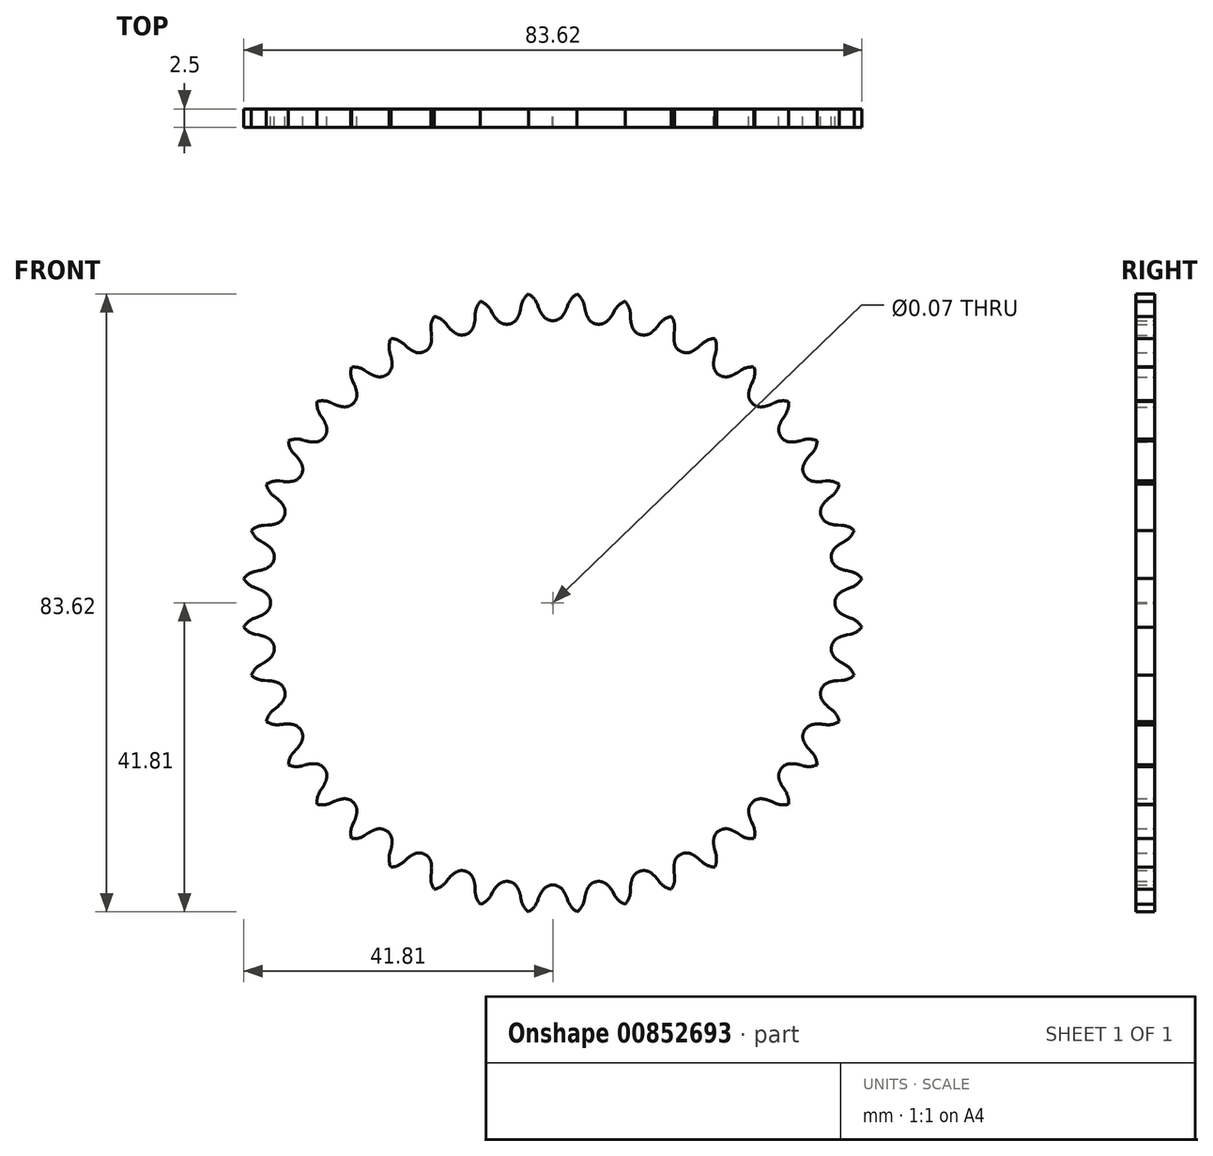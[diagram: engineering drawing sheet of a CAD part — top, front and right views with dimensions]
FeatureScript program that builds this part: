
annotation { "Feature Type Name" : "Feature", "Feature Type Description" : "" }
export const myFeature = defineFeature(function(context is Context, id is Id, definition is map)
    precondition{}
    {
        {
            var Q0;
            Q0=qCreatedBy(makeId("Front.planeOp"),FACE);
            var sketch = newSketch(context, id + "F0", { "sketchPlane" : qUnion([Q0]), "disableImprinting" : false});
            skCircle(sketch, "E0", {"center": v(0, 0) * mm, "radius": 0.04 * mm});
            skCircle(sketch, "E1", {"center": v(0, 0) * mm, "radius": 39.83 * mm, "construction": true});
            skLineSegment(sketch, "E2", {"start": v(0, 0) * mm, "end": v(0, 79.66) * mm, "construction": true});
            skLineSegment(sketch, "E3", {"start": v(-1.28, 39.83) * mm, "end": v(0, 39.83) * mm, "construction": true});
            skArc(sketch, "E4", {"start": v(-1.33, 38.84) * mm, "mid": v(-0.75, 38.35) * mm, "end": v(0, 38.17) * mm});
            skLineSegment(sketch, "E5.0", {"start": v(2.12, 0) * mm, "end": v(2.12, 79.66) * mm, "construction": true});
            skLineSegment(sketch, "E6.0", {"start": v(-1.75, 41.4) * mm, "end": v(1.4, 41.4) * mm, "construction": true});
            skLineSegment(sketch, "E7", {"start": v(2.57, 41.73) * mm, "end": v(-1.33, 38.84) * mm, "construction": true});
            skPoint(sketch, "E8", {"position": v(2.12, 41.4) * mm});
            skLineSegment(sketch, "E9", {"start": v(-1.92, 39.94) * mm, "end": v(2.12, 41.4) * mm, "construction": true});
            skArc(sketch, "E10", {"start": v(-1.92, 39.94) * mm, "mid": v(-1.67, 39.37) * mm, "end": v(-1.33, 38.84) * mm});
            skLineSegment(sketch, "E11", {"start": v(-1.92, 39.94) * mm, "end": v(-2.08, 40.38) * mm});
            skLineSegment(sketch, "E12.0", {"start": v(-4.6, 0) * mm, "end": v(-4.6, 79.66) * mm, "construction": true});
            skLineSegment(sketch, "E13.0", {"start": v(-3.1, 39.47) * mm, "end": v(0, 39.47) * mm, "construction": true});
            skArc(sketch, "E14", {"start": v(-4.6, 42.15) * mm, "mid": v(-6.5, 37.57) * mm, "end": v(-1.92, 39.47) * mm, "construction": true});
            skLineSegment(sketch, "E15", {"start": v(0, 0) * mm, "end": v(-0.91, 11.62) * mm, "construction": true});
            skLineSegment(sketch, "E16.trimOffspring", {"start": v(-1.7, 39.3) * mm, "end": v(-2.45, 41.4) * mm});
            skArc(sketch, "E17.trimOffspring", {"start": v(-2.08, 40.38) * mm, "mid": v(-2.56, 41.2) * mm, "end": v(-3.3, 41.8) * mm});
            skArc(sketch, "E18.trimOffspring", {"start": v(-1.94, 39.78) * mm, "mid": v(-1.94, 39.8) * mm, "end": v(-1.95, 39.83) * mm, "construction": true});
            skArc(sketch, "E19.trimOffspring", {"start": v(1.66, 39.8) * mm, "mid": v(-0.17, 41.48) * mm, "end": v(-1.62, 39.47) * mm, "construction": true});
            skArc(sketch, "E20.MirrorCS", {"start": v(1.33, 38.84) * mm, "mid": v(0.75, 38.35) * mm, "end": v(0, 38.17) * mm});
            skArc(sketch, "E21.MirrorCS", {"start": v(1.92, 39.94) * mm, "mid": v(1.67, 39.37) * mm, "end": v(1.33, 38.84) * mm});
            skLineSegment(sketch, "E22.MirrorCS", {"start": v(1.92, 39.94) * mm, "end": v(2.08, 40.38) * mm});
            skArc(sketch, "E23.MirrorCS", {"start": v(2.08, 40.38) * mm, "mid": v(2.56, 41.2) * mm, "end": v(3.3, 41.8) * mm});
            skArc(sketch, "E24.1.0", {"start": v(-8.37, 39.56) * mm, "mid": v(-8.97, 40.3) * mm, "end": v(-9.79, 40.78) * mm});
            skLineSegment(sketch, "E24.1.1", {"start": v(-8.14, 39.14) * mm, "end": v(-8.37, 39.56) * mm});
            skArc(sketch, "E24.1.2", {"start": v(-8.14, 39.14) * mm, "mid": v(-7.8, 38.62) * mm, "end": v(-7.4, 38.16) * mm});
            skArc(sketch, "E24.1.3", {"start": v(-7.4, 38.16) * mm, "mid": v(-6.74, 37.76) * mm, "end": v(-5.97, 37.7) * mm});
            skArc(sketch, "E24.1.4", {"start": v(-4.76, 38.57) * mm, "mid": v(-5.26, 38) * mm, "end": v(-5.97, 37.7) * mm});
            skArc(sketch, "E24.1.5", {"start": v(-4.35, 39.75) * mm, "mid": v(-4.51, 39.14) * mm, "end": v(-4.76, 38.57) * mm});
            skLineSegment(sketch, "E24.1.6", {"start": v(-4.35, 39.75) * mm, "end": v(-4.26, 40.2) * mm});
            skArc(sketch, "E24.1.7", {"start": v(-4.26, 40.2) * mm, "mid": v(-3.92, 41.1) * mm, "end": v(-3.3, 41.8) * mm});
            skArc(sketch, "E24.2.0", {"start": v(-14.46, 37.76) * mm, "mid": v(-15.16, 38.4) * mm, "end": v(-16.05, 38.74) * mm});
            skLineSegment(sketch, "E24.2.1", {"start": v(-14.17, 37.39) * mm, "end": v(-14.46, 37.76) * mm});
            skArc(sketch, "E24.2.2", {"start": v(-14.17, 37.39) * mm, "mid": v(-13.75, 36.93) * mm, "end": v(-13.27, 36.53) * mm});
            skArc(sketch, "E24.2.3", {"start": v(-13.27, 36.53) * mm, "mid": v(-12.56, 36.24) * mm, "end": v(-11.8, 36.3) * mm});
            skArc(sketch, "E24.2.4", {"start": v(-10.73, 37.35) * mm, "mid": v(-11.14, 36.7) * mm, "end": v(-11.8, 36.3) * mm});
            skArc(sketch, "E24.2.5", {"start": v(-10.51, 38.58) * mm, "mid": v(-10.58, 37.96) * mm, "end": v(-10.73, 37.35) * mm});
            skLineSegment(sketch, "E24.2.6", {"start": v(-10.51, 38.58) * mm, "end": v(-10.5, 39.05) * mm});
            skArc(sketch, "E24.2.7", {"start": v(-10.5, 39.05) * mm, "mid": v(-10.3, 39.98) * mm, "end": v(-9.79, 40.78) * mm});
            skArc(sketch, "E24.3.0", {"start": v(-20.19, 35.03) * mm, "mid": v(-20.98, 35.55) * mm, "end": v(-21.91, 35.76) * mm});
            skLineSegment(sketch, "E24.3.1", {"start": v(-19.84, 34.71) * mm, "end": v(-20.19, 35.03) * mm});
            skArc(sketch, "E24.3.2", {"start": v(-19.84, 34.71) * mm, "mid": v(-19.36, 34.32) * mm, "end": v(-18.82, 34) * mm});
            skArc(sketch, "E24.3.3", {"start": v(-18.82, 34) * mm, "mid": v(-18.08, 33.83) * mm, "end": v(-17.33, 34) * mm});
            skArc(sketch, "E24.3.4", {"start": v(-16.45, 35.21) * mm, "mid": v(-16.74, 34.5) * mm, "end": v(-17.33, 34) * mm});
            skArc(sketch, "E24.3.5", {"start": v(-16.42, 36.46) * mm, "mid": v(-16.39, 35.83) * mm, "end": v(-16.45, 35.21) * mm});
            skLineSegment(sketch, "E24.3.6", {"start": v(-16.42, 36.46) * mm, "end": v(-16.48, 36.92) * mm});
            skArc(sketch, "E24.3.7", {"start": v(-16.48, 36.92) * mm, "mid": v(-16.43, 37.87) * mm, "end": v(-16.05, 38.74) * mm});
            skArc(sketch, "E24.4.0", {"start": v(-25.42, 31.45) * mm, "mid": v(-26.29, 31.83) * mm, "end": v(-27.24, 31.89) * mm});
            skLineSegment(sketch, "E24.4.1", {"start": v(-25.03, 31.18) * mm, "end": v(-25.42, 31.45) * mm});
            skArc(sketch, "E24.4.2", {"start": v(-25.03, 31.18) * mm, "mid": v(-24.49, 30.87) * mm, "end": v(-23.91, 30.64) * mm});
            skArc(sketch, "E24.4.3", {"start": v(-23.91, 30.64) * mm, "mid": v(-23.14, 30.58) * mm, "end": v(-22.44, 30.88) * mm});
            skArc(sketch, "E24.4.4", {"start": v(-21.75, 32.2) * mm, "mid": v(-21.94, 31.46) * mm, "end": v(-22.44, 30.88) * mm});
            skArc(sketch, "E24.4.5", {"start": v(-21.92, 33.44) * mm, "mid": v(-21.8, 32.83) * mm, "end": v(-21.75, 32.2) * mm});
            skLineSegment(sketch, "E24.4.6", {"start": v(-21.92, 33.44) * mm, "end": v(-22.05, 33.9) * mm});
            skArc(sketch, "E24.4.7", {"start": v(-22.05, 33.9) * mm, "mid": v(-22.15, 34.84) * mm, "end": v(-21.91, 35.76) * mm});
            skArc(sketch, "E24.5.0", {"start": v(-30.03, 27.08) * mm, "mid": v(-30.94, 27.33) * mm, "end": v(-31.89, 27.24) * mm});
            skLineSegment(sketch, "E24.5.1", {"start": v(-29.6, 26.88) * mm, "end": v(-30.03, 27.08) * mm});
            skArc(sketch, "E24.5.2", {"start": v(-29.6, 26.88) * mm, "mid": v(-29.02, 26.66) * mm, "end": v(-28.4, 26.52) * mm});
            skArc(sketch, "E24.5.3", {"start": v(-28.4, 26.52) * mm, "mid": v(-27.64, 26.59) * mm, "end": v(-27, 27) * mm});
            skArc(sketch, "E24.5.4", {"start": v(-26.52, 28.4) * mm, "mid": v(-26.59, 27.64) * mm, "end": v(-27, 27) * mm});
            skArc(sketch, "E24.5.5", {"start": v(-26.88, 29.6) * mm, "mid": v(-26.66, 29.02) * mm, "end": v(-26.52, 28.4) * mm});
            skLineSegment(sketch, "E24.5.6", {"start": v(-26.88, 29.6) * mm, "end": v(-27.08, 30.03) * mm});
            skArc(sketch, "E24.5.7", {"start": v(-27.08, 30.03) * mm, "mid": v(-27.33, 30.94) * mm, "end": v(-27.24, 31.89) * mm});
            skArc(sketch, "E24.6.0", {"start": v(-33.9, 22.05) * mm, "mid": v(-34.84, 22.15) * mm, "end": v(-35.76, 21.91) * mm});
            skLineSegment(sketch, "E24.6.1", {"start": v(-33.44, 21.92) * mm, "end": v(-33.9, 22.05) * mm});
            skArc(sketch, "E24.6.2", {"start": v(-33.44, 21.92) * mm, "mid": v(-32.83, 21.8) * mm, "end": v(-32.2, 21.75) * mm});
            skArc(sketch, "E24.6.3", {"start": v(-32.2, 21.75) * mm, "mid": v(-31.46, 21.94) * mm, "end": v(-30.88, 22.44) * mm});
            skArc(sketch, "E24.6.4", {"start": v(-30.64, 23.91) * mm, "mid": v(-30.58, 23.14) * mm, "end": v(-30.88, 22.44) * mm});
            skArc(sketch, "E24.6.5", {"start": v(-31.18, 25.03) * mm, "mid": v(-30.87, 24.49) * mm, "end": v(-30.64, 23.91) * mm});
            skLineSegment(sketch, "E24.6.6", {"start": v(-31.18, 25.03) * mm, "end": v(-31.45, 25.42) * mm});
            skArc(sketch, "E24.6.7", {"start": v(-31.45, 25.42) * mm, "mid": v(-31.83, 26.29) * mm, "end": v(-31.89, 27.24) * mm});
            skArc(sketch, "E24.7.0", {"start": v(-36.92, 16.48) * mm, "mid": v(-37.87, 16.43) * mm, "end": v(-38.74, 16.05) * mm});
            skLineSegment(sketch, "E24.7.1", {"start": v(-36.46, 16.42) * mm, "end": v(-36.92, 16.48) * mm});
            skArc(sketch, "E24.7.2", {"start": v(-36.46, 16.42) * mm, "mid": v(-35.83, 16.39) * mm, "end": v(-35.21, 16.45) * mm});
            skArc(sketch, "E24.7.3", {"start": v(-35.21, 16.45) * mm, "mid": v(-34.5, 16.74) * mm, "end": v(-34, 17.33) * mm});
            skArc(sketch, "E24.7.4", {"start": v(-34, 18.82) * mm, "mid": v(-33.83, 18.08) * mm, "end": v(-34, 17.33) * mm});
            skArc(sketch, "E24.7.5", {"start": v(-34.71, 19.84) * mm, "mid": v(-34.32, 19.36) * mm, "end": v(-34, 18.82) * mm});
            skLineSegment(sketch, "E24.7.6", {"start": v(-34.71, 19.84) * mm, "end": v(-35.03, 20.19) * mm});
            skArc(sketch, "E24.7.7", {"start": v(-35.03, 20.19) * mm, "mid": v(-35.55, 20.98) * mm, "end": v(-35.76, 21.91) * mm});
            skArc(sketch, "E24.8.0", {"start": v(-39.05, 10.5) * mm, "mid": v(-39.98, 10.3) * mm, "end": v(-40.78, 9.79) * mm});
            skLineSegment(sketch, "E24.8.1", {"start": v(-38.58, 10.51) * mm, "end": v(-39.05, 10.5) * mm});
            skArc(sketch, "E24.8.2", {"start": v(-38.58, 10.51) * mm, "mid": v(-37.96, 10.58) * mm, "end": v(-37.35, 10.73) * mm});
            skArc(sketch, "E24.8.3", {"start": v(-37.35, 10.73) * mm, "mid": v(-36.7, 11.14) * mm, "end": v(-36.3, 11.8) * mm});
            skArc(sketch, "E24.8.4", {"start": v(-36.53, 13.27) * mm, "mid": v(-36.24, 12.56) * mm, "end": v(-36.3, 11.8) * mm});
            skArc(sketch, "E24.8.5", {"start": v(-37.39, 14.17) * mm, "mid": v(-36.93, 13.75) * mm, "end": v(-36.53, 13.27) * mm});
            skLineSegment(sketch, "E24.8.6", {"start": v(-37.39, 14.17) * mm, "end": v(-37.76, 14.46) * mm});
            skArc(sketch, "E24.8.7", {"start": v(-37.76, 14.46) * mm, "mid": v(-38.4, 15.16) * mm, "end": v(-38.74, 16.05) * mm});
            skArc(sketch, "E24.9.0", {"start": v(-40.2, 4.26) * mm, "mid": v(-41.1, 3.92) * mm, "end": v(-41.8, 3.3) * mm});
            skLineSegment(sketch, "E24.9.1", {"start": v(-39.75, 4.35) * mm, "end": v(-40.2, 4.26) * mm});
            skArc(sketch, "E24.9.2", {"start": v(-39.75, 4.35) * mm, "mid": v(-39.14, 4.51) * mm, "end": v(-38.57, 4.76) * mm});
            skArc(sketch, "E24.9.3", {"start": v(-38.57, 4.76) * mm, "mid": v(-38, 5.26) * mm, "end": v(-37.7, 5.97) * mm});
            skArc(sketch, "E24.9.4", {"start": v(-38.16, 7.4) * mm, "mid": v(-37.76, 6.74) * mm, "end": v(-37.7, 5.97) * mm});
            skArc(sketch, "E24.9.5", {"start": v(-39.14, 8.14) * mm, "mid": v(-38.62, 7.8) * mm, "end": v(-38.16, 7.4) * mm});
            skLineSegment(sketch, "E24.9.6", {"start": v(-39.14, 8.14) * mm, "end": v(-39.56, 8.37) * mm});
            skArc(sketch, "E24.9.7", {"start": v(-39.56, 8.37) * mm, "mid": v(-40.3, 8.97) * mm, "end": v(-40.78, 9.79) * mm});
            skLineSegment(sketch, "E25.4.10.0", {"start": v(-39.94, -1.92) * mm, "end": v(-40.38, -2.08) * mm});
            skArc(sketch, "E25.7.10.0", {"start": v(-39.94, -1.92) * mm, "mid": v(-39.37, -1.67) * mm, "end": v(-38.84, -1.33) * mm});
            skArc(sketch, "E25.11.10.0", {"start": v(-38.84, -1.33) * mm, "mid": v(-38.35, -0.75) * mm, "end": v(-38.17, 0) * mm});
            skArc(sketch, "E25.14.10.0", {"start": v(-40.38, -2.08) * mm, "mid": v(-41.2, -2.56) * mm, "end": v(-41.8, -3.3) * mm});
            skArc(sketch, "E25.15.10.0", {"start": v(-38.84, 1.33) * mm, "mid": v(-38.35, 0.75) * mm, "end": v(-38.17, 0) * mm});
            skArc(sketch, "E25.19.10.0", {"start": v(-39.94, 1.92) * mm, "mid": v(-39.37, 1.67) * mm, "end": v(-38.84, 1.33) * mm});
            skLineSegment(sketch, "E25.23.10.0", {"start": v(-39.94, 1.92) * mm, "end": v(-40.38, 2.08) * mm});
            skArc(sketch, "E25.26.10.0", {"start": v(-40.38, 2.08) * mm, "mid": v(-41.2, 2.56) * mm, "end": v(-41.8, 3.3) * mm});
            skLineSegment(sketch, "E25.4.11.0", {"start": v(-39.14, -8.14) * mm, "end": v(-39.56, -8.37) * mm});
            skArc(sketch, "E25.7.11.0", {"start": v(-39.14, -8.14) * mm, "mid": v(-38.62, -7.8) * mm, "end": v(-38.16, -7.4) * mm});
            skArc(sketch, "E25.11.11.0", {"start": v(-38.16, -7.4) * mm, "mid": v(-37.76, -6.74) * mm, "end": v(-37.7, -5.97) * mm});
            skArc(sketch, "E25.14.11.0", {"start": v(-39.56, -8.37) * mm, "mid": v(-40.3, -8.97) * mm, "end": v(-40.78, -9.79) * mm});
            skArc(sketch, "E25.15.11.0", {"start": v(-38.57, -4.76) * mm, "mid": v(-38, -5.26) * mm, "end": v(-37.7, -5.97) * mm});
            skArc(sketch, "E25.19.11.0", {"start": v(-39.75, -4.35) * mm, "mid": v(-39.14, -4.51) * mm, "end": v(-38.57, -4.76) * mm});
            skLineSegment(sketch, "E25.23.11.0", {"start": v(-39.75, -4.35) * mm, "end": v(-40.2, -4.26) * mm});
            skArc(sketch, "E25.26.11.0", {"start": v(-40.2, -4.26) * mm, "mid": v(-41.1, -3.92) * mm, "end": v(-41.8, -3.3) * mm});
            skLineSegment(sketch, "E25.4.12.0", {"start": v(-37.39, -14.17) * mm, "end": v(-37.76, -14.46) * mm});
            skArc(sketch, "E25.7.12.0", {"start": v(-37.39, -14.17) * mm, "mid": v(-36.93, -13.75) * mm, "end": v(-36.53, -13.27) * mm});
            skArc(sketch, "E25.11.12.0", {"start": v(-36.53, -13.27) * mm, "mid": v(-36.24, -12.56) * mm, "end": v(-36.3, -11.8) * mm});
            skArc(sketch, "E25.14.12.0", {"start": v(-37.76, -14.46) * mm, "mid": v(-38.4, -15.16) * mm, "end": v(-38.74, -16.05) * mm});
            skArc(sketch, "E25.15.12.0", {"start": v(-37.35, -10.73) * mm, "mid": v(-36.7, -11.14) * mm, "end": v(-36.3, -11.8) * mm});
            skArc(sketch, "E25.19.12.0", {"start": v(-38.58, -10.51) * mm, "mid": v(-37.96, -10.58) * mm, "end": v(-37.35, -10.73) * mm});
            skLineSegment(sketch, "E25.23.12.0", {"start": v(-38.58, -10.51) * mm, "end": v(-39.05, -10.5) * mm});
            skArc(sketch, "E25.26.12.0", {"start": v(-39.05, -10.5) * mm, "mid": v(-39.98, -10.3) * mm, "end": v(-40.78, -9.79) * mm});
            skLineSegment(sketch, "E25.4.13.0", {"start": v(-34.71, -19.84) * mm, "end": v(-35.03, -20.19) * mm});
            skArc(sketch, "E25.7.13.0", {"start": v(-34.71, -19.84) * mm, "mid": v(-34.32, -19.36) * mm, "end": v(-34, -18.82) * mm});
            skArc(sketch, "E25.11.13.0", {"start": v(-34, -18.82) * mm, "mid": v(-33.83, -18.08) * mm, "end": v(-34, -17.33) * mm});
            skArc(sketch, "E25.14.13.0", {"start": v(-35.03, -20.19) * mm, "mid": v(-35.55, -20.98) * mm, "end": v(-35.76, -21.91) * mm});
            skArc(sketch, "E25.15.13.0", {"start": v(-35.21, -16.45) * mm, "mid": v(-34.5, -16.74) * mm, "end": v(-34, -17.33) * mm});
            skArc(sketch, "E25.19.13.0", {"start": v(-36.46, -16.42) * mm, "mid": v(-35.83, -16.39) * mm, "end": v(-35.21, -16.45) * mm});
            skLineSegment(sketch, "E25.23.13.0", {"start": v(-36.46, -16.42) * mm, "end": v(-36.92, -16.48) * mm});
            skArc(sketch, "E25.26.13.0", {"start": v(-36.92, -16.48) * mm, "mid": v(-37.87, -16.43) * mm, "end": v(-38.74, -16.05) * mm});
            skLineSegment(sketch, "E25.4.14.0", {"start": v(-31.18, -25.03) * mm, "end": v(-31.45, -25.42) * mm});
            skArc(sketch, "E25.7.14.0", {"start": v(-31.18, -25.03) * mm, "mid": v(-30.87, -24.49) * mm, "end": v(-30.64, -23.91) * mm});
            skArc(sketch, "E25.11.14.0", {"start": v(-30.64, -23.91) * mm, "mid": v(-30.58, -23.14) * mm, "end": v(-30.88, -22.44) * mm});
            skArc(sketch, "E25.14.14.0", {"start": v(-31.45, -25.42) * mm, "mid": v(-31.83, -26.29) * mm, "end": v(-31.89, -27.24) * mm});
            skArc(sketch, "E25.15.14.0", {"start": v(-32.2, -21.75) * mm, "mid": v(-31.46, -21.94) * mm, "end": v(-30.88, -22.44) * mm});
            skArc(sketch, "E25.19.14.0", {"start": v(-33.44, -21.92) * mm, "mid": v(-32.83, -21.8) * mm, "end": v(-32.2, -21.75) * mm});
            skLineSegment(sketch, "E25.23.14.0", {"start": v(-33.44, -21.92) * mm, "end": v(-33.9, -22.05) * mm});
            skArc(sketch, "E25.26.14.0", {"start": v(-33.9, -22.05) * mm, "mid": v(-34.84, -22.15) * mm, "end": v(-35.76, -21.91) * mm});
            skLineSegment(sketch, "E25.4.15.0", {"start": v(-26.88, -29.6) * mm, "end": v(-27.08, -30.03) * mm});
            skArc(sketch, "E25.7.15.0", {"start": v(-26.88, -29.6) * mm, "mid": v(-26.66, -29.02) * mm, "end": v(-26.52, -28.4) * mm});
            skArc(sketch, "E25.11.15.0", {"start": v(-26.52, -28.4) * mm, "mid": v(-26.59, -27.64) * mm, "end": v(-27, -27) * mm});
            skArc(sketch, "E25.14.15.0", {"start": v(-27.08, -30.03) * mm, "mid": v(-27.33, -30.94) * mm, "end": v(-27.24, -31.89) * mm});
            skArc(sketch, "E25.15.15.0", {"start": v(-28.4, -26.52) * mm, "mid": v(-27.64, -26.59) * mm, "end": v(-27, -27) * mm});
            skArc(sketch, "E25.19.15.0", {"start": v(-29.6, -26.88) * mm, "mid": v(-29.02, -26.66) * mm, "end": v(-28.4, -26.52) * mm});
            skLineSegment(sketch, "E25.23.15.0", {"start": v(-29.6, -26.88) * mm, "end": v(-30.03, -27.08) * mm});
            skArc(sketch, "E25.26.15.0", {"start": v(-30.03, -27.08) * mm, "mid": v(-30.94, -27.33) * mm, "end": v(-31.89, -27.24) * mm});
            skLineSegment(sketch, "E25.4.16.0", {"start": v(-21.92, -33.44) * mm, "end": v(-22.05, -33.9) * mm});
            skArc(sketch, "E25.7.16.0", {"start": v(-21.92, -33.44) * mm, "mid": v(-21.8, -32.83) * mm, "end": v(-21.75, -32.2) * mm});
            skArc(sketch, "E25.11.16.0", {"start": v(-21.75, -32.2) * mm, "mid": v(-21.94, -31.46) * mm, "end": v(-22.44, -30.88) * mm});
            skArc(sketch, "E25.14.16.0", {"start": v(-22.05, -33.9) * mm, "mid": v(-22.15, -34.84) * mm, "end": v(-21.91, -35.76) * mm});
            skArc(sketch, "E25.15.16.0", {"start": v(-23.91, -30.64) * mm, "mid": v(-23.14, -30.58) * mm, "end": v(-22.44, -30.88) * mm});
            skArc(sketch, "E25.19.16.0", {"start": v(-25.03, -31.18) * mm, "mid": v(-24.49, -30.87) * mm, "end": v(-23.91, -30.64) * mm});
            skLineSegment(sketch, "E25.23.16.0", {"start": v(-25.03, -31.18) * mm, "end": v(-25.42, -31.45) * mm});
            skArc(sketch, "E25.26.16.0", {"start": v(-25.42, -31.45) * mm, "mid": v(-26.29, -31.83) * mm, "end": v(-27.24, -31.89) * mm});
            skLineSegment(sketch, "E25.4.17.0", {"start": v(-16.42, -36.46) * mm, "end": v(-16.48, -36.92) * mm});
            skArc(sketch, "E25.7.17.0", {"start": v(-16.42, -36.46) * mm, "mid": v(-16.39, -35.83) * mm, "end": v(-16.45, -35.21) * mm});
            skArc(sketch, "E25.11.17.0", {"start": v(-16.45, -35.21) * mm, "mid": v(-16.74, -34.5) * mm, "end": v(-17.33, -34) * mm});
            skArc(sketch, "E25.14.17.0", {"start": v(-16.48, -36.92) * mm, "mid": v(-16.43, -37.87) * mm, "end": v(-16.05, -38.74) * mm});
            skArc(sketch, "E25.15.17.0", {"start": v(-18.82, -34) * mm, "mid": v(-18.08, -33.83) * mm, "end": v(-17.33, -34) * mm});
            skArc(sketch, "E25.19.17.0", {"start": v(-19.84, -34.71) * mm, "mid": v(-19.36, -34.32) * mm, "end": v(-18.82, -34) * mm});
            skLineSegment(sketch, "E25.23.17.0", {"start": v(-19.84, -34.71) * mm, "end": v(-20.19, -35.03) * mm});
            skArc(sketch, "E25.26.17.0", {"start": v(-20.19, -35.03) * mm, "mid": v(-20.98, -35.55) * mm, "end": v(-21.91, -35.76) * mm});
            skLineSegment(sketch, "E25.4.18.0", {"start": v(-10.51, -38.58) * mm, "end": v(-10.5, -39.05) * mm});
            skArc(sketch, "E25.7.18.0", {"start": v(-10.51, -38.58) * mm, "mid": v(-10.58, -37.96) * mm, "end": v(-10.73, -37.35) * mm});
            skArc(sketch, "E25.11.18.0", {"start": v(-10.73, -37.35) * mm, "mid": v(-11.14, -36.7) * mm, "end": v(-11.8, -36.3) * mm});
            skArc(sketch, "E25.14.18.0", {"start": v(-10.5, -39.05) * mm, "mid": v(-10.3, -39.98) * mm, "end": v(-9.79, -40.78) * mm});
            skArc(sketch, "E25.15.18.0", {"start": v(-13.27, -36.53) * mm, "mid": v(-12.56, -36.24) * mm, "end": v(-11.8, -36.3) * mm});
            skArc(sketch, "E25.19.18.0", {"start": v(-14.17, -37.39) * mm, "mid": v(-13.75, -36.93) * mm, "end": v(-13.27, -36.53) * mm});
            skLineSegment(sketch, "E25.23.18.0", {"start": v(-14.17, -37.39) * mm, "end": v(-14.46, -37.76) * mm});
            skArc(sketch, "E25.26.18.0", {"start": v(-14.46, -37.76) * mm, "mid": v(-15.16, -38.4) * mm, "end": v(-16.05, -38.74) * mm});
            skLineSegment(sketch, "E25.4.19.0", {"start": v(-4.35, -39.75) * mm, "end": v(-4.26, -40.2) * mm});
            skArc(sketch, "E25.7.19.0", {"start": v(-4.35, -39.75) * mm, "mid": v(-4.51, -39.14) * mm, "end": v(-4.76, -38.57) * mm});
            skArc(sketch, "E25.11.19.0", {"start": v(-4.76, -38.57) * mm, "mid": v(-5.26, -38) * mm, "end": v(-5.97, -37.7) * mm});
            skArc(sketch, "E25.14.19.0", {"start": v(-4.26, -40.2) * mm, "mid": v(-3.92, -41.1) * mm, "end": v(-3.3, -41.8) * mm});
            skArc(sketch, "E25.15.19.0", {"start": v(-7.4, -38.16) * mm, "mid": v(-6.74, -37.76) * mm, "end": v(-5.97, -37.7) * mm});
            skArc(sketch, "E25.19.19.0", {"start": v(-8.14, -39.14) * mm, "mid": v(-7.8, -38.62) * mm, "end": v(-7.4, -38.16) * mm});
            skLineSegment(sketch, "E25.23.19.0", {"start": v(-8.14, -39.14) * mm, "end": v(-8.37, -39.56) * mm});
            skArc(sketch, "E25.26.19.0", {"start": v(-8.37, -39.56) * mm, "mid": v(-8.97, -40.3) * mm, "end": v(-9.79, -40.78) * mm});
            skLineSegment(sketch, "E25.4.20.0", {"start": v(1.92, -39.94) * mm, "end": v(2.08, -40.38) * mm});
            skArc(sketch, "E25.7.20.0", {"start": v(1.92, -39.94) * mm, "mid": v(1.67, -39.37) * mm, "end": v(1.33, -38.84) * mm});
            skArc(sketch, "E25.11.20.0", {"start": v(1.33, -38.84) * mm, "mid": v(0.75, -38.35) * mm, "end": v(0, -38.17) * mm});
            skArc(sketch, "E25.14.20.0", {"start": v(2.08, -40.38) * mm, "mid": v(2.56, -41.2) * mm, "end": v(3.3, -41.8) * mm});
            skArc(sketch, "E25.15.20.0", {"start": v(-1.33, -38.84) * mm, "mid": v(-0.75, -38.35) * mm, "end": v(0, -38.17) * mm});
            skArc(sketch, "E25.19.20.0", {"start": v(-1.92, -39.94) * mm, "mid": v(-1.67, -39.37) * mm, "end": v(-1.33, -38.84) * mm});
            skLineSegment(sketch, "E25.23.20.0", {"start": v(-1.92, -39.94) * mm, "end": v(-2.08, -40.38) * mm});
            skArc(sketch, "E25.26.20.0", {"start": v(-2.08, -40.38) * mm, "mid": v(-2.56, -41.2) * mm, "end": v(-3.3, -41.8) * mm});
            skLineSegment(sketch, "E25.4.21.0", {"start": v(8.14, -39.14) * mm, "end": v(8.37, -39.56) * mm});
            skArc(sketch, "E25.7.21.0", {"start": v(8.14, -39.14) * mm, "mid": v(7.8, -38.62) * mm, "end": v(7.4, -38.16) * mm});
            skArc(sketch, "E25.11.21.0", {"start": v(7.4, -38.16) * mm, "mid": v(6.74, -37.76) * mm, "end": v(5.97, -37.7) * mm});
            skArc(sketch, "E25.14.21.0", {"start": v(8.37, -39.56) * mm, "mid": v(8.97, -40.3) * mm, "end": v(9.79, -40.78) * mm});
            skArc(sketch, "E25.15.21.0", {"start": v(4.76, -38.57) * mm, "mid": v(5.26, -38) * mm, "end": v(5.97, -37.7) * mm});
            skArc(sketch, "E25.19.21.0", {"start": v(4.35, -39.75) * mm, "mid": v(4.51, -39.14) * mm, "end": v(4.76, -38.57) * mm});
            skLineSegment(sketch, "E25.23.21.0", {"start": v(4.35, -39.75) * mm, "end": v(4.26, -40.2) * mm});
            skArc(sketch, "E25.26.21.0", {"start": v(4.26, -40.2) * mm, "mid": v(3.92, -41.1) * mm, "end": v(3.3, -41.8) * mm});
            skLineSegment(sketch, "E25.4.22.0", {"start": v(14.17, -37.39) * mm, "end": v(14.46, -37.76) * mm});
            skArc(sketch, "E25.7.22.0", {"start": v(14.17, -37.39) * mm, "mid": v(13.75, -36.93) * mm, "end": v(13.27, -36.53) * mm});
            skArc(sketch, "E25.11.22.0", {"start": v(13.27, -36.53) * mm, "mid": v(12.56, -36.24) * mm, "end": v(11.8, -36.3) * mm});
            skArc(sketch, "E25.14.22.0", {"start": v(14.46, -37.76) * mm, "mid": v(15.16, -38.4) * mm, "end": v(16.05, -38.74) * mm});
            skArc(sketch, "E25.15.22.0", {"start": v(10.73, -37.35) * mm, "mid": v(11.14, -36.7) * mm, "end": v(11.8, -36.3) * mm});
            skArc(sketch, "E25.19.22.0", {"start": v(10.51, -38.58) * mm, "mid": v(10.58, -37.96) * mm, "end": v(10.73, -37.35) * mm});
            skLineSegment(sketch, "E25.23.22.0", {"start": v(10.51, -38.58) * mm, "end": v(10.5, -39.05) * mm});
            skArc(sketch, "E25.26.22.0", {"start": v(10.5, -39.05) * mm, "mid": v(10.3, -39.98) * mm, "end": v(9.79, -40.78) * mm});
            skLineSegment(sketch, "E25.4.23.0", {"start": v(19.84, -34.71) * mm, "end": v(20.19, -35.03) * mm});
            skArc(sketch, "E25.7.23.0", {"start": v(19.84, -34.71) * mm, "mid": v(19.36, -34.32) * mm, "end": v(18.82, -34) * mm});
            skArc(sketch, "E25.11.23.0", {"start": v(18.82, -34) * mm, "mid": v(18.08, -33.83) * mm, "end": v(17.33, -34) * mm});
            skArc(sketch, "E25.14.23.0", {"start": v(20.19, -35.03) * mm, "mid": v(20.98, -35.55) * mm, "end": v(21.91, -35.76) * mm});
            skArc(sketch, "E25.15.23.0", {"start": v(16.45, -35.21) * mm, "mid": v(16.74, -34.5) * mm, "end": v(17.33, -34) * mm});
            skArc(sketch, "E25.19.23.0", {"start": v(16.42, -36.46) * mm, "mid": v(16.39, -35.83) * mm, "end": v(16.45, -35.21) * mm});
            skLineSegment(sketch, "E25.23.23.0", {"start": v(16.42, -36.46) * mm, "end": v(16.48, -36.92) * mm});
            skArc(sketch, "E25.26.23.0", {"start": v(16.48, -36.92) * mm, "mid": v(16.43, -37.87) * mm, "end": v(16.05, -38.74) * mm});
            skLineSegment(sketch, "E25.4.24.0", {"start": v(25.03, -31.18) * mm, "end": v(25.42, -31.45) * mm});
            skArc(sketch, "E25.7.24.0", {"start": v(25.03, -31.18) * mm, "mid": v(24.49, -30.87) * mm, "end": v(23.91, -30.64) * mm});
            skArc(sketch, "E25.11.24.0", {"start": v(23.91, -30.64) * mm, "mid": v(23.14, -30.58) * mm, "end": v(22.44, -30.88) * mm});
            skArc(sketch, "E25.14.24.0", {"start": v(25.42, -31.45) * mm, "mid": v(26.29, -31.83) * mm, "end": v(27.24, -31.89) * mm});
            skArc(sketch, "E25.15.24.0", {"start": v(21.75, -32.2) * mm, "mid": v(21.94, -31.46) * mm, "end": v(22.44, -30.88) * mm});
            skArc(sketch, "E25.19.24.0", {"start": v(21.92, -33.44) * mm, "mid": v(21.8, -32.83) * mm, "end": v(21.75, -32.2) * mm});
            skLineSegment(sketch, "E25.23.24.0", {"start": v(21.92, -33.44) * mm, "end": v(22.05, -33.9) * mm});
            skArc(sketch, "E25.26.24.0", {"start": v(22.05, -33.9) * mm, "mid": v(22.15, -34.84) * mm, "end": v(21.91, -35.76) * mm});
            skLineSegment(sketch, "E25.4.25.0", {"start": v(29.6, -26.88) * mm, "end": v(30.03, -27.08) * mm});
            skArc(sketch, "E25.7.25.0", {"start": v(29.6, -26.88) * mm, "mid": v(29.02, -26.66) * mm, "end": v(28.4, -26.52) * mm});
            skArc(sketch, "E25.11.25.0", {"start": v(28.4, -26.52) * mm, "mid": v(27.64, -26.59) * mm, "end": v(27, -27) * mm});
            skArc(sketch, "E25.14.25.0", {"start": v(30.03, -27.08) * mm, "mid": v(30.94, -27.33) * mm, "end": v(31.89, -27.24) * mm});
            skArc(sketch, "E25.15.25.0", {"start": v(26.52, -28.4) * mm, "mid": v(26.59, -27.64) * mm, "end": v(27, -27) * mm});
            skArc(sketch, "E25.19.25.0", {"start": v(26.88, -29.6) * mm, "mid": v(26.66, -29.02) * mm, "end": v(26.52, -28.4) * mm});
            skLineSegment(sketch, "E25.23.25.0", {"start": v(26.88, -29.6) * mm, "end": v(27.08, -30.03) * mm});
            skArc(sketch, "E25.26.25.0", {"start": v(27.08, -30.03) * mm, "mid": v(27.33, -30.94) * mm, "end": v(27.24, -31.89) * mm});
            skLineSegment(sketch, "E25.4.26.0", {"start": v(33.44, -21.92) * mm, "end": v(33.9, -22.05) * mm});
            skArc(sketch, "E25.7.26.0", {"start": v(33.44, -21.92) * mm, "mid": v(32.83, -21.8) * mm, "end": v(32.2, -21.75) * mm});
            skArc(sketch, "E25.11.26.0", {"start": v(32.2, -21.75) * mm, "mid": v(31.46, -21.94) * mm, "end": v(30.88, -22.44) * mm});
            skArc(sketch, "E25.14.26.0", {"start": v(33.9, -22.05) * mm, "mid": v(34.84, -22.15) * mm, "end": v(35.76, -21.91) * mm});
            skArc(sketch, "E25.15.26.0", {"start": v(30.64, -23.91) * mm, "mid": v(30.58, -23.14) * mm, "end": v(30.88, -22.44) * mm});
            skArc(sketch, "E25.19.26.0", {"start": v(31.18, -25.03) * mm, "mid": v(30.87, -24.49) * mm, "end": v(30.64, -23.91) * mm});
            skLineSegment(sketch, "E25.23.26.0", {"start": v(31.18, -25.03) * mm, "end": v(31.45, -25.42) * mm});
            skArc(sketch, "E25.26.26.0", {"start": v(31.45, -25.42) * mm, "mid": v(31.83, -26.29) * mm, "end": v(31.89, -27.24) * mm});
            skLineSegment(sketch, "E25.4.27.0", {"start": v(36.46, -16.42) * mm, "end": v(36.92, -16.48) * mm});
            skArc(sketch, "E25.7.27.0", {"start": v(36.46, -16.42) * mm, "mid": v(35.83, -16.39) * mm, "end": v(35.21, -16.45) * mm});
            skArc(sketch, "E25.11.27.0", {"start": v(35.21, -16.45) * mm, "mid": v(34.5, -16.74) * mm, "end": v(34, -17.33) * mm});
            skArc(sketch, "E25.14.27.0", {"start": v(36.92, -16.48) * mm, "mid": v(37.87, -16.43) * mm, "end": v(38.74, -16.05) * mm});
            skArc(sketch, "E25.15.27.0", {"start": v(34, -18.82) * mm, "mid": v(33.83, -18.08) * mm, "end": v(34, -17.33) * mm});
            skArc(sketch, "E25.19.27.0", {"start": v(34.71, -19.84) * mm, "mid": v(34.32, -19.36) * mm, "end": v(34, -18.82) * mm});
            skLineSegment(sketch, "E25.23.27.0", {"start": v(34.71, -19.84) * mm, "end": v(35.03, -20.19) * mm});
            skArc(sketch, "E25.26.27.0", {"start": v(35.03, -20.19) * mm, "mid": v(35.55, -20.98) * mm, "end": v(35.76, -21.91) * mm});
            skLineSegment(sketch, "E25.4.28.0", {"start": v(38.58, -10.51) * mm, "end": v(39.05, -10.5) * mm});
            skArc(sketch, "E25.7.28.0", {"start": v(38.58, -10.51) * mm, "mid": v(37.96, -10.58) * mm, "end": v(37.35, -10.73) * mm});
            skArc(sketch, "E25.11.28.0", {"start": v(37.35, -10.73) * mm, "mid": v(36.7, -11.14) * mm, "end": v(36.3, -11.8) * mm});
            skArc(sketch, "E25.14.28.0", {"start": v(39.05, -10.5) * mm, "mid": v(39.98, -10.3) * mm, "end": v(40.78, -9.79) * mm});
            skArc(sketch, "E25.15.28.0", {"start": v(36.53, -13.27) * mm, "mid": v(36.24, -12.56) * mm, "end": v(36.3, -11.8) * mm});
            skArc(sketch, "E25.19.28.0", {"start": v(37.39, -14.17) * mm, "mid": v(36.93, -13.75) * mm, "end": v(36.53, -13.27) * mm});
            skLineSegment(sketch, "E25.23.28.0", {"start": v(37.39, -14.17) * mm, "end": v(37.76, -14.46) * mm});
            skArc(sketch, "E25.26.28.0", {"start": v(37.76, -14.46) * mm, "mid": v(38.4, -15.16) * mm, "end": v(38.74, -16.05) * mm});
            skLineSegment(sketch, "E25.4.29.0", {"start": v(39.75, -4.35) * mm, "end": v(40.2, -4.26) * mm});
            skArc(sketch, "E25.7.29.0", {"start": v(39.75, -4.35) * mm, "mid": v(39.14, -4.51) * mm, "end": v(38.57, -4.76) * mm});
            skArc(sketch, "E25.11.29.0", {"start": v(38.57, -4.76) * mm, "mid": v(38, -5.26) * mm, "end": v(37.7, -5.97) * mm});
            skArc(sketch, "E25.14.29.0", {"start": v(40.2, -4.26) * mm, "mid": v(41.1, -3.92) * mm, "end": v(41.8, -3.3) * mm});
            skArc(sketch, "E25.15.29.0", {"start": v(38.16, -7.4) * mm, "mid": v(37.76, -6.74) * mm, "end": v(37.7, -5.97) * mm});
            skArc(sketch, "E25.19.29.0", {"start": v(39.14, -8.14) * mm, "mid": v(38.62, -7.8) * mm, "end": v(38.16, -7.4) * mm});
            skLineSegment(sketch, "E25.23.29.0", {"start": v(39.14, -8.14) * mm, "end": v(39.56, -8.37) * mm});
            skArc(sketch, "E25.26.29.0", {"start": v(39.56, -8.37) * mm, "mid": v(40.3, -8.97) * mm, "end": v(40.78, -9.79) * mm});
            skLineSegment(sketch, "E25.4.30.0", {"start": v(39.94, 1.92) * mm, "end": v(40.38, 2.08) * mm});
            skArc(sketch, "E25.7.30.0", {"start": v(39.94, 1.92) * mm, "mid": v(39.37, 1.67) * mm, "end": v(38.84, 1.33) * mm});
            skArc(sketch, "E25.11.30.0", {"start": v(38.84, 1.33) * mm, "mid": v(38.35, 0.75) * mm, "end": v(38.17, 0) * mm});
            skArc(sketch, "E25.14.30.0", {"start": v(40.38, 2.08) * mm, "mid": v(41.2, 2.56) * mm, "end": v(41.8, 3.3) * mm});
            skArc(sketch, "E25.15.30.0", {"start": v(38.84, -1.33) * mm, "mid": v(38.35, -0.75) * mm, "end": v(38.17, 0) * mm});
            skArc(sketch, "E25.19.30.0", {"start": v(39.94, -1.92) * mm, "mid": v(39.37, -1.67) * mm, "end": v(38.84, -1.33) * mm});
            skLineSegment(sketch, "E25.23.30.0", {"start": v(39.94, -1.92) * mm, "end": v(40.38, -2.08) * mm});
            skArc(sketch, "E25.26.30.0", {"start": v(40.38, -2.08) * mm, "mid": v(41.2, -2.56) * mm, "end": v(41.8, -3.3) * mm});
            skLineSegment(sketch, "E25.4.31.0", {"start": v(39.14, 8.14) * mm, "end": v(39.56, 8.37) * mm});
            skArc(sketch, "E25.7.31.0", {"start": v(39.14, 8.14) * mm, "mid": v(38.62, 7.8) * mm, "end": v(38.16, 7.4) * mm});
            skArc(sketch, "E25.11.31.0", {"start": v(38.16, 7.4) * mm, "mid": v(37.76, 6.74) * mm, "end": v(37.7, 5.97) * mm});
            skArc(sketch, "E25.14.31.0", {"start": v(39.56, 8.37) * mm, "mid": v(40.3, 8.97) * mm, "end": v(40.78, 9.79) * mm});
            skArc(sketch, "E25.15.31.0", {"start": v(38.57, 4.76) * mm, "mid": v(38, 5.26) * mm, "end": v(37.7, 5.97) * mm});
            skArc(sketch, "E25.19.31.0", {"start": v(39.75, 4.35) * mm, "mid": v(39.14, 4.51) * mm, "end": v(38.57, 4.76) * mm});
            skLineSegment(sketch, "E25.23.31.0", {"start": v(39.75, 4.35) * mm, "end": v(40.2, 4.26) * mm});
            skArc(sketch, "E25.26.31.0", {"start": v(40.2, 4.26) * mm, "mid": v(41.1, 3.92) * mm, "end": v(41.8, 3.3) * mm});
            skLineSegment(sketch, "E25.4.32.0", {"start": v(37.39, 14.17) * mm, "end": v(37.76, 14.46) * mm});
            skArc(sketch, "E25.7.32.0", {"start": v(37.39, 14.17) * mm, "mid": v(36.93, 13.75) * mm, "end": v(36.53, 13.27) * mm});
            skArc(sketch, "E25.11.32.0", {"start": v(36.53, 13.27) * mm, "mid": v(36.24, 12.56) * mm, "end": v(36.3, 11.8) * mm});
            skArc(sketch, "E25.14.32.0", {"start": v(37.76, 14.46) * mm, "mid": v(38.4, 15.16) * mm, "end": v(38.74, 16.05) * mm});
            skArc(sketch, "E25.15.32.0", {"start": v(37.35, 10.73) * mm, "mid": v(36.7, 11.14) * mm, "end": v(36.3, 11.8) * mm});
            skArc(sketch, "E25.19.32.0", {"start": v(38.58, 10.51) * mm, "mid": v(37.96, 10.58) * mm, "end": v(37.35, 10.73) * mm});
            skLineSegment(sketch, "E25.23.32.0", {"start": v(38.58, 10.51) * mm, "end": v(39.05, 10.5) * mm});
            skArc(sketch, "E25.26.32.0", {"start": v(39.05, 10.5) * mm, "mid": v(39.98, 10.3) * mm, "end": v(40.78, 9.79) * mm});
            skLineSegment(sketch, "E25.4.33.0", {"start": v(34.71, 19.84) * mm, "end": v(35.03, 20.19) * mm});
            skArc(sketch, "E25.7.33.0", {"start": v(34.71, 19.84) * mm, "mid": v(34.32, 19.36) * mm, "end": v(34, 18.82) * mm});
            skArc(sketch, "E25.11.33.0", {"start": v(34, 18.82) * mm, "mid": v(33.83, 18.08) * mm, "end": v(34, 17.33) * mm});
            skArc(sketch, "E25.14.33.0", {"start": v(35.03, 20.19) * mm, "mid": v(35.55, 20.98) * mm, "end": v(35.76, 21.91) * mm});
            skArc(sketch, "E25.15.33.0", {"start": v(35.21, 16.45) * mm, "mid": v(34.5, 16.74) * mm, "end": v(34, 17.33) * mm});
            skArc(sketch, "E25.19.33.0", {"start": v(36.46, 16.42) * mm, "mid": v(35.83, 16.39) * mm, "end": v(35.21, 16.45) * mm});
            skLineSegment(sketch, "E25.23.33.0", {"start": v(36.46, 16.42) * mm, "end": v(36.92, 16.48) * mm});
            skArc(sketch, "E25.26.33.0", {"start": v(36.92, 16.48) * mm, "mid": v(37.87, 16.43) * mm, "end": v(38.74, 16.05) * mm});
            skLineSegment(sketch, "E25.4.34.0", {"start": v(31.18, 25.03) * mm, "end": v(31.45, 25.42) * mm});
            skArc(sketch, "E25.7.34.0", {"start": v(31.18, 25.03) * mm, "mid": v(30.87, 24.49) * mm, "end": v(30.64, 23.91) * mm});
            skArc(sketch, "E25.11.34.0", {"start": v(30.64, 23.91) * mm, "mid": v(30.58, 23.14) * mm, "end": v(30.88, 22.44) * mm});
            skArc(sketch, "E25.14.34.0", {"start": v(31.45, 25.42) * mm, "mid": v(31.83, 26.29) * mm, "end": v(31.89, 27.24) * mm});
            skArc(sketch, "E25.15.34.0", {"start": v(32.2, 21.75) * mm, "mid": v(31.46, 21.94) * mm, "end": v(30.88, 22.44) * mm});
            skArc(sketch, "E25.19.34.0", {"start": v(33.44, 21.92) * mm, "mid": v(32.83, 21.8) * mm, "end": v(32.2, 21.75) * mm});
            skLineSegment(sketch, "E25.23.34.0", {"start": v(33.44, 21.92) * mm, "end": v(33.9, 22.05) * mm});
            skArc(sketch, "E25.26.34.0", {"start": v(33.9, 22.05) * mm, "mid": v(34.84, 22.15) * mm, "end": v(35.76, 21.91) * mm});
            skLineSegment(sketch, "E25.4.35.0", {"start": v(26.88, 29.6) * mm, "end": v(27.08, 30.03) * mm});
            skArc(sketch, "E25.7.35.0", {"start": v(26.88, 29.6) * mm, "mid": v(26.66, 29.02) * mm, "end": v(26.52, 28.4) * mm});
            skArc(sketch, "E25.11.35.0", {"start": v(26.52, 28.4) * mm, "mid": v(26.59, 27.64) * mm, "end": v(27, 27) * mm});
            skArc(sketch, "E25.14.35.0", {"start": v(27.08, 30.03) * mm, "mid": v(27.33, 30.94) * mm, "end": v(27.24, 31.89) * mm});
            skArc(sketch, "E25.15.35.0", {"start": v(28.4, 26.52) * mm, "mid": v(27.64, 26.59) * mm, "end": v(27, 27) * mm});
            skArc(sketch, "E25.19.35.0", {"start": v(29.6, 26.88) * mm, "mid": v(29.02, 26.66) * mm, "end": v(28.4, 26.52) * mm});
            skLineSegment(sketch, "E25.23.35.0", {"start": v(29.6, 26.88) * mm, "end": v(30.03, 27.08) * mm});
            skArc(sketch, "E25.26.35.0", {"start": v(30.03, 27.08) * mm, "mid": v(30.94, 27.33) * mm, "end": v(31.89, 27.24) * mm});
            skLineSegment(sketch, "E25.4.36.0", {"start": v(21.92, 33.44) * mm, "end": v(22.05, 33.9) * mm});
            skArc(sketch, "E25.7.36.0", {"start": v(21.92, 33.44) * mm, "mid": v(21.8, 32.83) * mm, "end": v(21.75, 32.2) * mm});
            skArc(sketch, "E25.11.36.0", {"start": v(21.75, 32.2) * mm, "mid": v(21.94, 31.46) * mm, "end": v(22.44, 30.88) * mm});
            skArc(sketch, "E25.14.36.0", {"start": v(22.05, 33.9) * mm, "mid": v(22.15, 34.84) * mm, "end": v(21.91, 35.76) * mm});
            skArc(sketch, "E25.15.36.0", {"start": v(23.91, 30.64) * mm, "mid": v(23.14, 30.58) * mm, "end": v(22.44, 30.88) * mm});
            skArc(sketch, "E25.19.36.0", {"start": v(25.03, 31.18) * mm, "mid": v(24.49, 30.87) * mm, "end": v(23.91, 30.64) * mm});
            skLineSegment(sketch, "E25.23.36.0", {"start": v(25.03, 31.18) * mm, "end": v(25.42, 31.45) * mm});
            skArc(sketch, "E25.26.36.0", {"start": v(25.42, 31.45) * mm, "mid": v(26.29, 31.83) * mm, "end": v(27.24, 31.89) * mm});
            skLineSegment(sketch, "E25.4.37.0", {"start": v(16.42, 36.46) * mm, "end": v(16.48, 36.92) * mm});
            skArc(sketch, "E25.7.37.0", {"start": v(16.42, 36.46) * mm, "mid": v(16.39, 35.83) * mm, "end": v(16.45, 35.21) * mm});
            skArc(sketch, "E25.11.37.0", {"start": v(16.45, 35.21) * mm, "mid": v(16.74, 34.5) * mm, "end": v(17.33, 34) * mm});
            skArc(sketch, "E25.14.37.0", {"start": v(16.48, 36.92) * mm, "mid": v(16.43, 37.87) * mm, "end": v(16.05, 38.74) * mm});
            skArc(sketch, "E25.15.37.0", {"start": v(18.82, 34) * mm, "mid": v(18.08, 33.83) * mm, "end": v(17.33, 34) * mm});
            skArc(sketch, "E25.19.37.0", {"start": v(19.84, 34.71) * mm, "mid": v(19.36, 34.32) * mm, "end": v(18.82, 34) * mm});
            skLineSegment(sketch, "E25.23.37.0", {"start": v(19.84, 34.71) * mm, "end": v(20.19, 35.03) * mm});
            skArc(sketch, "E25.26.37.0", {"start": v(20.19, 35.03) * mm, "mid": v(20.98, 35.55) * mm, "end": v(21.91, 35.76) * mm});
            skLineSegment(sketch, "E25.4.38.0", {"start": v(10.51, 38.58) * mm, "end": v(10.5, 39.05) * mm});
            skArc(sketch, "E25.7.38.0", {"start": v(10.51, 38.58) * mm, "mid": v(10.58, 37.96) * mm, "end": v(10.73, 37.35) * mm});
            skArc(sketch, "E25.11.38.0", {"start": v(10.73, 37.35) * mm, "mid": v(11.14, 36.7) * mm, "end": v(11.8, 36.3) * mm});
            skArc(sketch, "E25.14.38.0", {"start": v(10.5, 39.05) * mm, "mid": v(10.3, 39.98) * mm, "end": v(9.79, 40.78) * mm});
            skArc(sketch, "E25.15.38.0", {"start": v(13.27, 36.53) * mm, "mid": v(12.56, 36.24) * mm, "end": v(11.8, 36.3) * mm});
            skArc(sketch, "E25.19.38.0", {"start": v(14.17, 37.39) * mm, "mid": v(13.75, 36.93) * mm, "end": v(13.27, 36.53) * mm});
            skLineSegment(sketch, "E25.23.38.0", {"start": v(14.17, 37.39) * mm, "end": v(14.46, 37.76) * mm});
            skArc(sketch, "E25.26.38.0", {"start": v(14.46, 37.76) * mm, "mid": v(15.16, 38.4) * mm, "end": v(16.05, 38.74) * mm});
            skLineSegment(sketch, "E25.4.39.0", {"start": v(4.35, 39.75) * mm, "end": v(4.26, 40.2) * mm});
            skArc(sketch, "E25.7.39.0", {"start": v(4.35, 39.75) * mm, "mid": v(4.51, 39.14) * mm, "end": v(4.76, 38.57) * mm});
            skArc(sketch, "E25.11.39.0", {"start": v(4.76, 38.57) * mm, "mid": v(5.26, 38) * mm, "end": v(5.97, 37.7) * mm});
            skArc(sketch, "E25.14.39.0", {"start": v(4.26, 40.2) * mm, "mid": v(3.92, 41.1) * mm, "end": v(3.3, 41.8) * mm});
            skArc(sketch, "E25.15.39.0", {"start": v(7.4, 38.16) * mm, "mid": v(6.74, 37.76) * mm, "end": v(5.97, 37.7) * mm});
            skArc(sketch, "E25.19.39.0", {"start": v(8.14, 39.14) * mm, "mid": v(7.8, 38.62) * mm, "end": v(7.4, 38.16) * mm});
            skLineSegment(sketch, "E25.23.39.0", {"start": v(8.14, 39.14) * mm, "end": v(8.37, 39.56) * mm});
            skArc(sketch, "E25.26.39.0", {"start": v(8.37, 39.56) * mm, "mid": v(8.97, 40.3) * mm, "end": v(9.79, 40.78) * mm});
            skSolve(sketch);
        }
        {
            var Q0;
            Q0=makeQuery(id+"F0.imprint","IMPRINT",FACE,{"disambiguationData":[TD([[makeQuery(id+"F0.imprint","IMPRINT",EDGE,{"derivedFrom":sQuery(id+"F0.wireOp",EDGE,"E0")}),-1.0]])]});
            var Q1;
            Q1=sQuery(id+"F0.wireOp",EDGE,"E1");
            extrude(context, id + "F1", {"entities" : qUnion([Q0]), "flatOperationType" : FlatOperationType.REMOVE, "surfaceEntities" : qUnion([Q1]), "depth" : 2.5 * mm, "offsetDistance" : 25 * mm, "domain" : OperationDomain.MODEL});
        }
    });
